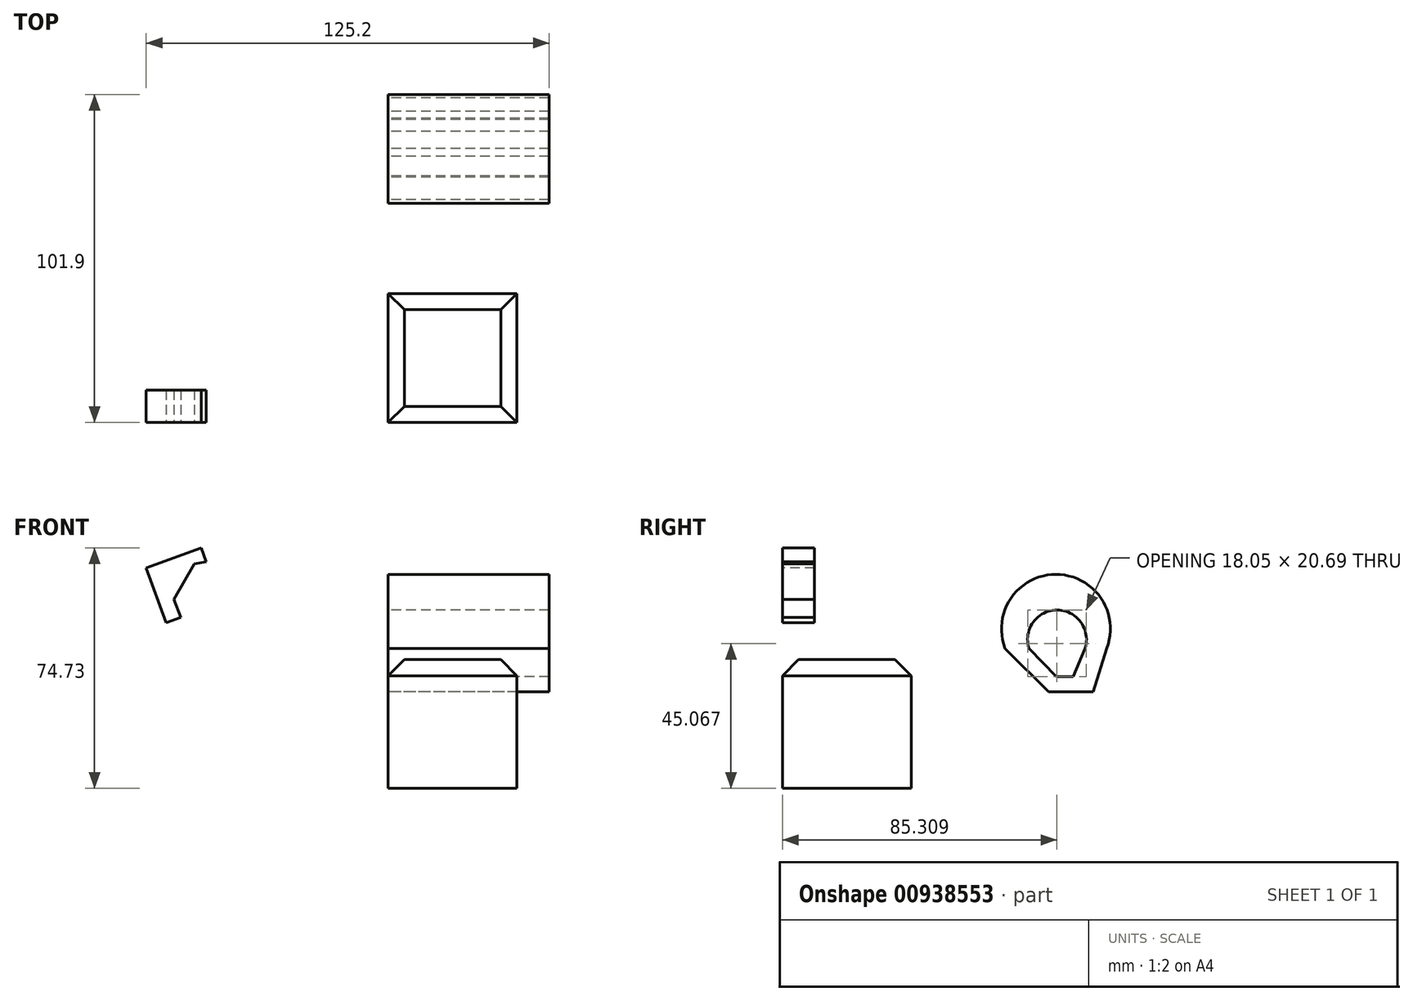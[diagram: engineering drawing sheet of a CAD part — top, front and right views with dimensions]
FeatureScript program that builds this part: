
annotation { "Feature Type Name" : "Feature", "Feature Type Description" : "" }
export const myFeature = defineFeature(function(context is Context, id is Id, definition is map)
    precondition{}
    {
        {
            var Q0;
            Q0=qCreatedBy(makeId("Front.planeOp"),FACE);
            var sketch = newSketch(context, id + "F0", { "sketchPlane" : qUnion([Q0])});
            skLineSegment(sketch, "E0.bottom", {"start": v(0, 0) * mm, "end": v(40, 0) * mm});
            skLineSegment(sketch, "E0.top", {"start": v(0, 40) * mm, "end": v(40, 40) * mm});
            skLineSegment(sketch, "E0.left", {"start": v(0, 0) * mm, "end": v(0, 40) * mm});
            skLineSegment(sketch, "E0.right", {"start": v(40, 0) * mm, "end": v(40, 40) * mm});
            skSolve(sketch);
        }
        {
            var Q0;
            Q0 = qSketchRegion(id + "F0", true);
            extrude(context, id + "F1", {"entities" : qUnion([Q0]), "depth" : 40 * mm, "offsetDistance" : 25 * mm});
        }
        {
            var Q0;
            Q0=makeQuery(id+"F1.opExtrude","CAP_FACE",FACE,{"disambiguationData":[OSD([sQuery(id+"F0.wireOp",EDGE,"E0.bottom"),sQuery(id+"F0.wireOp",EDGE,"E0.top"),sQuery(id+"F0.wireOp",EDGE,"E0.left"),sQuery(id+"F0.wireOp",EDGE,"E0.right")])],"isStart":false});
            var sketch = newSketch(context, id + "F2", { "sketchPlane" : qUnion([Q0])});
            skLineSegment(sketch, "E1", {"start": v(8.66, 37.61) * mm, "end": v(8.66, 15) * mm});
            skLineSegment(sketch, "E2.bottom", {"start": v(17, 35.69) * mm, "end": v(40, 35.69) * mm});
            skLineSegment(sketch, "E2.top", {"start": v(17, 24.62) * mm, "end": v(40, 24.62) * mm});
            skLineSegment(sketch, "E2.left", {"start": v(17, 35.69) * mm, "end": v(17, 24.62) * mm});
            skLineSegment(sketch, "E2.right", {"start": v(40, 35.69) * mm, "end": v(40, 24.62) * mm});
            skCircle(sketch, "E3.cCircle", {"center": v(-63.56, 63.09) * mm, "radius": 9.08 * mm, "construction": true});
            skLineSegment(sketch, "E3.0", {"start": v(-51.93, 57.66) * mm, "end": v(-69, 51.45) * mm});
            skLineSegment(sketch, "E3.1", {"start": v(-69, 51.45) * mm, "end": v(-75.2, 68.52) * mm});
            skLineSegment(sketch, "E3.2", {"start": v(-75.2, 68.52) * mm, "end": v(-58.13, 74.73) * mm});
            skLineSegment(sketch, "E3.3", {"start": v(-58.13, 74.73) * mm, "end": v(-51.93, 57.66) * mm});
            skPoint(sketch, "E3.0.midPoint", {"position": v(-60.46, 54.56) * mm});
            skCircle(sketch, "E4.cCircle", {"center": v(-51.93, 57.66) * mm, "radius": 13.3 * mm, "construction": true});
            skLineSegment(sketch, "E4.0", {"start": v(-49.68, 43.07) * mm, "end": v(-61.93, 46.8) * mm});
            skLineSegment(sketch, "E4.1", {"start": v(-61.93, 46.8) * mm, "end": v(-66.65, 58.71) * mm});
            skLineSegment(sketch, "E4.2", {"start": v(-66.65, 58.71) * mm, "end": v(-60.28, 69.83) * mm});
            skLineSegment(sketch, "E4.3", {"start": v(-60.28, 69.83) * mm, "end": v(-47.62, 71.78) * mm});
            skLineSegment(sketch, "E4.4", {"start": v(-47.62, 71.78) * mm, "end": v(-38.2, 63.1) * mm});
            skLineSegment(sketch, "E4.5", {"start": v(-38.2, 63.1) * mm, "end": v(-39.12, 50.32) * mm});
            skLineSegment(sketch, "E4.6", {"start": v(-39.12, 50.32) * mm, "end": v(-49.68, 43.07) * mm});
            skPoint(sketch, "E4.0.midPoint", {"position": v(-55.8, 44.94) * mm});
            skCircle(sketch, "E5.cCircle", {"center": v(-41.38, 39.82) * mm, "radius": 12.65 * mm, "construction": true});
            skLineSegment(sketch, "E5.0", {"start": v(-39.83, 14.56) * mm, "end": v(-64.02, 51.1) * mm});
            skLineSegment(sketch, "E5.1", {"start": v(-64.02, 51.1) * mm, "end": v(-20.28, 53.78) * mm});
            skLineSegment(sketch, "E5.2", {"start": v(-20.28, 53.78) * mm, "end": v(-39.83, 14.56) * mm});
            skPoint(sketch, "E5.0.midPoint", {"position": v(-51.93, 32.84) * mm});
            skCircle(sketch, "E6.cCircle", {"center": v(-65.74, 23.84) * mm, "radius": 5.82 * mm, "construction": true});
            skLineSegment(sketch, "E6.0", {"start": v(-59.22, 22.22) * mm, "end": v(-63.88, 17.39) * mm});
            skLineSegment(sketch, "E6.1", {"start": v(-63.88, 17.39) * mm, "end": v(-70.4, 19) * mm});
            skLineSegment(sketch, "E6.2", {"start": v(-70.4, 19) * mm, "end": v(-72.25, 25.45) * mm});
            skLineSegment(sketch, "E6.3", {"start": v(-72.25, 25.45) * mm, "end": v(-67.6, 30.3) * mm});
            skLineSegment(sketch, "E6.4", {"start": v(-67.6, 30.3) * mm, "end": v(-61.08, 28.67) * mm});
            skLineSegment(sketch, "E6.5", {"start": v(-61.08, 28.67) * mm, "end": v(-59.22, 22.22) * mm});
            skPoint(sketch, "E6.0.midPoint", {"position": v(-61.55, 19.8) * mm});
            skSolve(sketch);
        }
        {
            var Q0;
            {var subQ4=sQuery(id+"F2.wireOp",EDGE,"E3.1");Q0=makeQuery(id+"F2.imprint","IMPRINT",FACE,{"disambiguationData":[TD([[makeQuery(id+"F2.imprint","IMPRINT",EDGE,{"derivedFrom":subQ4}),-1.0]])]});}
            extrude(context, id + "F3", {"entities" : qUnion([Q0]), "depth" : -10 * mm, "offsetDistance" : 25 * mm});
        }
        {
            var Q0;
            Q0=qCreatedBy(makeId("Right.planeOp"),FACE);
            var sketch = newSketch(context, id + "F4", { "sketchPlane" : qUnion([Q0])});
            skLineSegment(sketch, "E7", {"start": v(60.79, 43.55) * mm, "end": v(56.62, 30.07) * mm});
            skLineSegment(sketch, "E8", {"start": v(56.62, 30.07) * mm, "end": v(42.66, 30.07) * mm});
            skLineSegment(sketch, "E9", {"start": v(42.66, 30.07) * mm, "end": v(29.2, 43.55) * mm});
            skLineSegment(sketch, "E10", {"start": v(60.79, 43.55) * mm, "end": v(54.05, 43.55) * mm});
            skLineSegment(sketch, "E11", {"start": v(54.05, 43.55) * mm, "end": v(50.36, 34.72) * mm});
            skLineSegment(sketch, "E12", {"start": v(50.36, 34.72) * mm, "end": v(45.07, 34.72) * mm});
            skLineSegment(sketch, "E13", {"start": v(45.07, 34.72) * mm, "end": v(36.57, 43.55) * mm});
            skLineSegment(sketch, "E14", {"start": v(36.57, 43.55) * mm, "end": v(29.2, 43.55) * mm});
            skArc(sketch, "E15", {"start": v(54.05, 43.55) * mm, "mid": v(45.3, 55.4) * mm, "end": v(36.57, 43.55) * mm});
            skArc(sketch, "E16", {"start": v(60.79, 43.55) * mm, "mid": v(44.99, 66.5) * mm, "end": v(29.2, 43.55) * mm});
            skSolve(sketch);
        }
        {
            var Q0;
            Q0=makeQuery(id+"F4.imprint","IMPRINT",FACE,{"disambiguationData":[TD([[makeQuery(id+"F4.imprint","IMPRINT",EDGE,{"derivedFrom":sQuery(id+"F4.wireOp",EDGE,"E10")}),-1.0]])]});
            var Q1;
            Q1=makeQuery(id+"F4.imprint","IMPRINT",FACE,{"disambiguationData":[TD([[makeQuery(id+"F4.imprint","IMPRINT",EDGE,{"derivedFrom":sQuery(id+"F4.wireOp",EDGE,"E7")}),-1.0]])]});
            extrude(context, id + "F5", {"entities" : qUnion([Q0, Q1]), "depth" : 50 * mm, "offsetDistance" : 25 * mm});
        }
        {
            var Q0;
            Q0=makeQuery(id+"F1.opExtrude","SWEPT_FACE",FACE,{"disambiguationData":[OSD([sQuery(id+"F0.wireOp",EDGE,"E0.top")])]});
            chamfer(context, id + "F6", {"entities" : qUnion([Q0]), "width" : 5 * mm, "tangentPropagation" : true});
        }
    });
